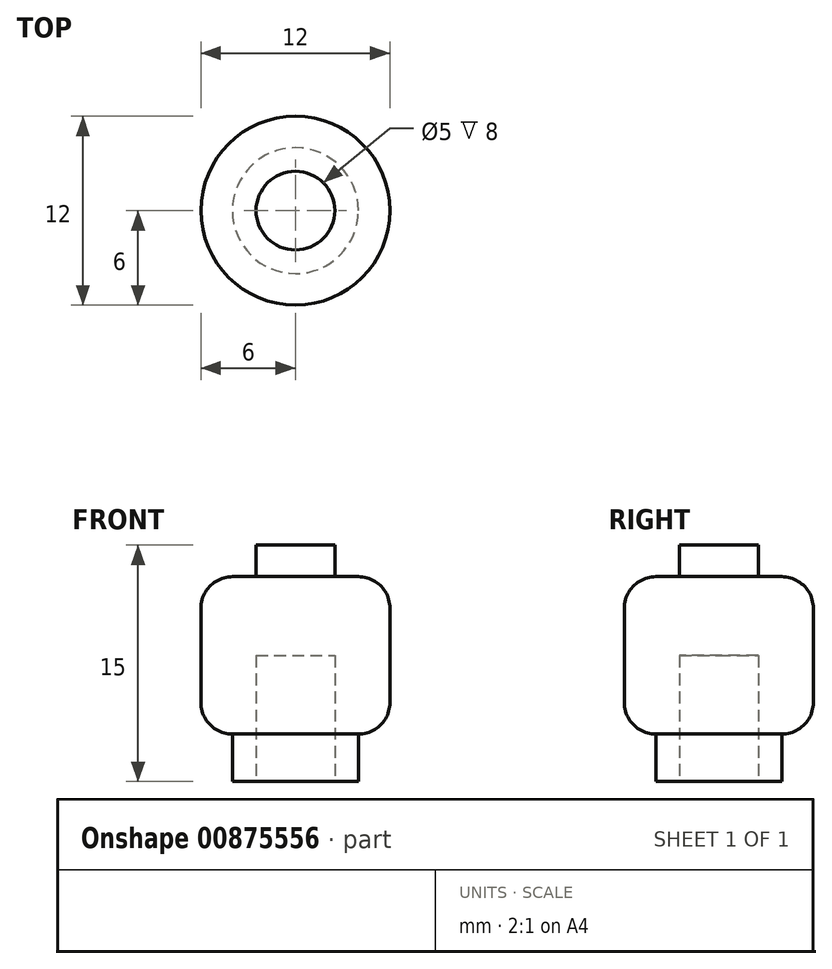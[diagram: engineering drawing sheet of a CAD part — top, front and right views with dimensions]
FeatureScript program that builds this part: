
annotation { "Feature Type Name" : "Feature", "Feature Type Description" : "" }
export const myFeature = defineFeature(function(context is Context, id is Id, definition is map)
    precondition{}
    {
        {
            var Q0;
            Q0=qCreatedBy(makeId("Top.planeOp"),FACE);
            var sketch = newSketch(context, id + "F0", { "sketchPlane" : qUnion([Q0])});
            skCircle(sketch, "E0", {"center": v(0, 0) * mm, "radius": 4 * mm});
            skSolve(sketch);
        }
        {
            var Q0;
            Q0=makeQuery(id+"F0.imprint","IMPRINT",FACE,{"disambiguationData":[TD([[makeQuery(id+"F0.imprint","IMPRINT",EDGE,{"derivedFrom":sQuery(id+"F0.wireOp",EDGE,"E0")}),1.0]])]});
            extrude(context, id + "F1", {"entities" : qUnion([Q0]), "depth" : 3 * mm, "offsetDistance" : 25 * mm});
        }
        {
            var Q0;
            Q0=makeQuery(id+"F1.opExtrude","CAP_FACE",FACE,{"disambiguationData":[OSD([sQuery(id+"F0.wireOp",EDGE,"E0")])],"isStart":false});
            var sketch = newSketch(context, id + "F2", { "sketchPlane" : qUnion([Q0])});
            skCircle(sketch, "E1", {"center": v(0, 0) * mm, "radius": 6 * mm});
            skSolve(sketch);
        }
        {
            var Q0;
            Q0 = qSketchRegion(id + "F2", true);
            var Q1;
            Q1 = qSketchRegion(id + "F4", true);
            extrude(context, id + "F3", {"entities" : qUnion([Q0, Q1]), "operationType" : NewBodyOperationType.ADD, "depth" : 10 * mm, "offsetDistance" : 25 * mm});
        }
        {
            var Q0;
            Q0=makeQuery(id+"F3.opExtrude","CAP_FACE",FACE,{"disambiguationData":[OSD([sQuery(id+"F2.wireOp",EDGE,"E1")])],"isStart":false});
            var sketch = newSketch(context, id + "F4", { "sketchPlane" : qUnion([Q0])});
            skCircle(sketch, "E2", {"center": v(0, 0) * mm, "radius": 2.5 * mm});
            skSolve(sketch);
        }
        {
            var Q0;
            Q0 = qSketchRegion(id + "F4", true);
            extrude(context, id + "F5", {"entities" : qUnion([Q0]), "operationType" : NewBodyOperationType.ADD, "depth" : 2 * mm, "offsetDistance" : 25 * mm});
        }
        {
            var Q0;
            Q0=makeQuery(id+"F3.opExtrude","CAP_EDGE",EDGE,{"disambiguationData":[OSD([sQuery(id+"F2.wireOp",EDGE,"E1")])],"isStart":false});
            var Q1;
            Q1=makeQuery(id+"F3.opExtrude","CAP_EDGE",EDGE,{"disambiguationData":[OSD([sQuery(id+"F2.wireOp",EDGE,"E1")])],"isStart":true});
            fillet(context, id + "F6", {"entities" : qUnion([Q0, Q1]), "radius" : 2 * mm, "tangentPropagation" : true, "allowEdgeOverflow" : false});
        }
        {
            var Q0;
            Q0=makeQuery(id+"F1.opExtrude","CAP_FACE",FACE,{"disambiguationData":[OSD([sQuery(id+"F0.wireOp",EDGE,"E0")])],"isStart":true});
            var sketch = newSketch(context, id + "F7", { "sketchPlane" : qUnion([Q0])});
            skCircle(sketch, "E3", {"center": v(0, 0) * mm, "radius": 2.5 * mm});
            skSolve(sketch);
        }
        {
            var Q0;
            Q0 = qSketchRegion(id + "F7", true);
            extrude(context, id + "F8", {"entities" : qUnion([Q0]), "operationType" : NewBodyOperationType.REMOVE, "oppositeDirection" : true, "depth" : 8 * mm, "offsetDistance" : 25 * mm});
        }
    });
